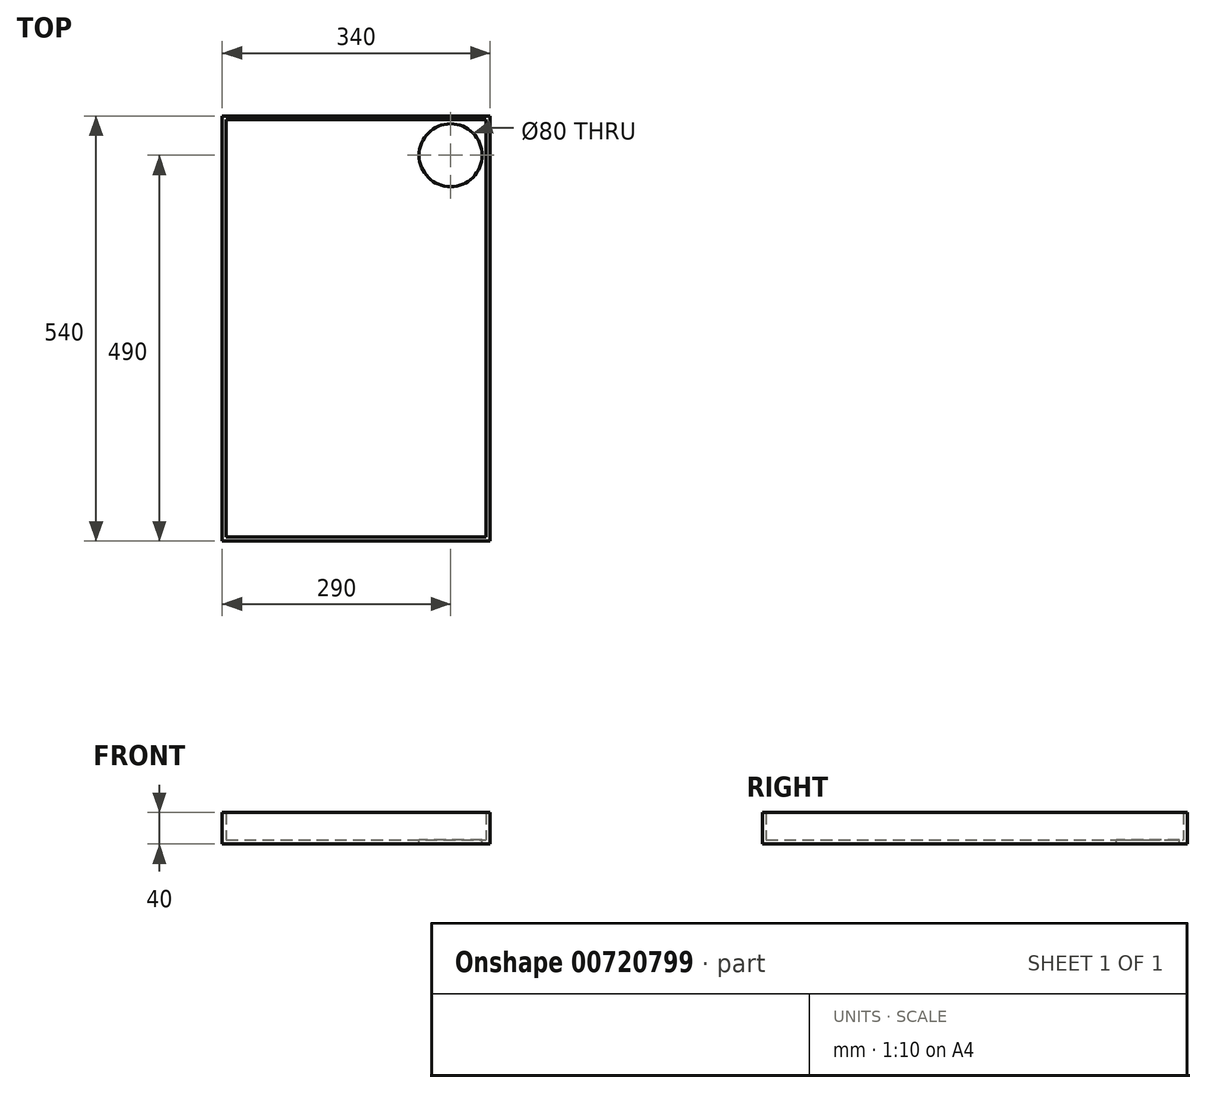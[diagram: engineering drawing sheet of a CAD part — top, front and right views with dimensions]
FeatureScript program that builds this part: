
annotation { "Feature Type Name" : "Feature", "Feature Type Description" : "" }
export const myFeature = defineFeature(function(context is Context, id is Id, definition is map)
    precondition{}
    {
        {
            var Q0;
            Q0=qCreatedBy(makeId("Top.planeOp"),FACE);
            var sketch = newSketch(context, id + "F0", { "sketchPlane" : qUnion([Q0])});
            skLineSegment(sketch, "E0", {"start": v(-170, 0) * mm, "end": v(-170, 270) * mm});
            skLineSegment(sketch, "E1.bottom", {"start": v(-170, 270) * mm, "end": v(170, 270) * mm});
            skLineSegment(sketch, "E1.top", {"start": v(-170, -270) * mm, "end": v(170, -270) * mm});
            skLineSegment(sketch, "E1.left", {"start": v(-170, 270) * mm, "end": v(-170, -270) * mm});
            skLineSegment(sketch, "E1.right", {"start": v(170, 270) * mm, "end": v(170, -270) * mm});
            skSolve(sketch);
        }
        {
            var Q0;
            {var subQ0=sQuery(id+"F0.wireOp",EDGE,"E1.bottom");Q0=makeQuery(id+"F0.imprint","IMPRINT",FACE,{"disambiguationData":[TD([[makeQuery(id+"F0.imprint","IMPRINT",EDGE,{"derivedFrom":subQ0}),-1.0]])]});}
            extrude(context, id + "F1", {"entities" : qUnion([Q0]), "depth" : 40 * mm, "offsetDistance" : 25 * mm});
        }
        {
            var Q0;
            Q0=makeQuery(id+"F1.opExtrude","CAP_FACE",FACE,{"disambiguationData":[OSD([sQuery(id+"F0.wireOp",EDGE,"E1.bottom"),sQuery(id+"F0.wireOp",EDGE,"E1.top"),sQuery(id+"F0.wireOp",EDGE,"E1.left"),sQuery(id+"F0.wireOp",EDGE,"E1.right")])],"isStart":false});
            shell(context, id + "F2", {"entities" : qUnion([Q0]), "thickness" : 5 * mm});
        }
        {
            var Q0;
            Q0=makeQuery(id+"F2.opShell","OFFSET_FACE",FACE,{"disambiguationData":[OSD([sQuery(id+"F0.wireOp",EDGE,"E1.bottom"),sQuery(id+"F0.wireOp",EDGE,"E1.top"),sQuery(id+"F0.wireOp",EDGE,"E1.left"),sQuery(id+"F0.wireOp",EDGE,"E1.right")])]});
            var sketch = newSketch(context, id + "F3", { "sketchPlane" : qUnion([Q0])});
            skCircle(sketch, "E2", {"center": v(120, 220) * mm, "radius": 40 * mm});
            skSolve(sketch);
        }
        {
            var Q0;
            Q0=sQuery(id+"F3.wireOp",VERTEX,"E2.center");
            var Q1;
            Q1=makeQuery(id+"F1.opExtrude","SWEPT_BODY",BODY,{"disambiguationData":[OSD([sQuery(id+"F0.wireOp",EDGE,"E1.bottom"),sQuery(id+"F0.wireOp",EDGE,"E1.top"),sQuery(id+"F0.wireOp",EDGE,"E1.left"),sQuery(id+"F0.wireOp",EDGE,"E1.right")])]});
            hole(context, id + "F4", {"style" : HoleStyle.SIMPLE, "endStyle" : HoleEndStyle.BLIND, "holeDiameter" : 80 * mm, "majorDiameter" : 5 * mm, "holeDepth" : 60 * mm, "isTappedThrough" : true, "tappedDepth" : 12 * mm, "tapClearance" : 3, "locations" : qUnion([Q0]), "scope" : qUnion([Q1])});
        }
    });
